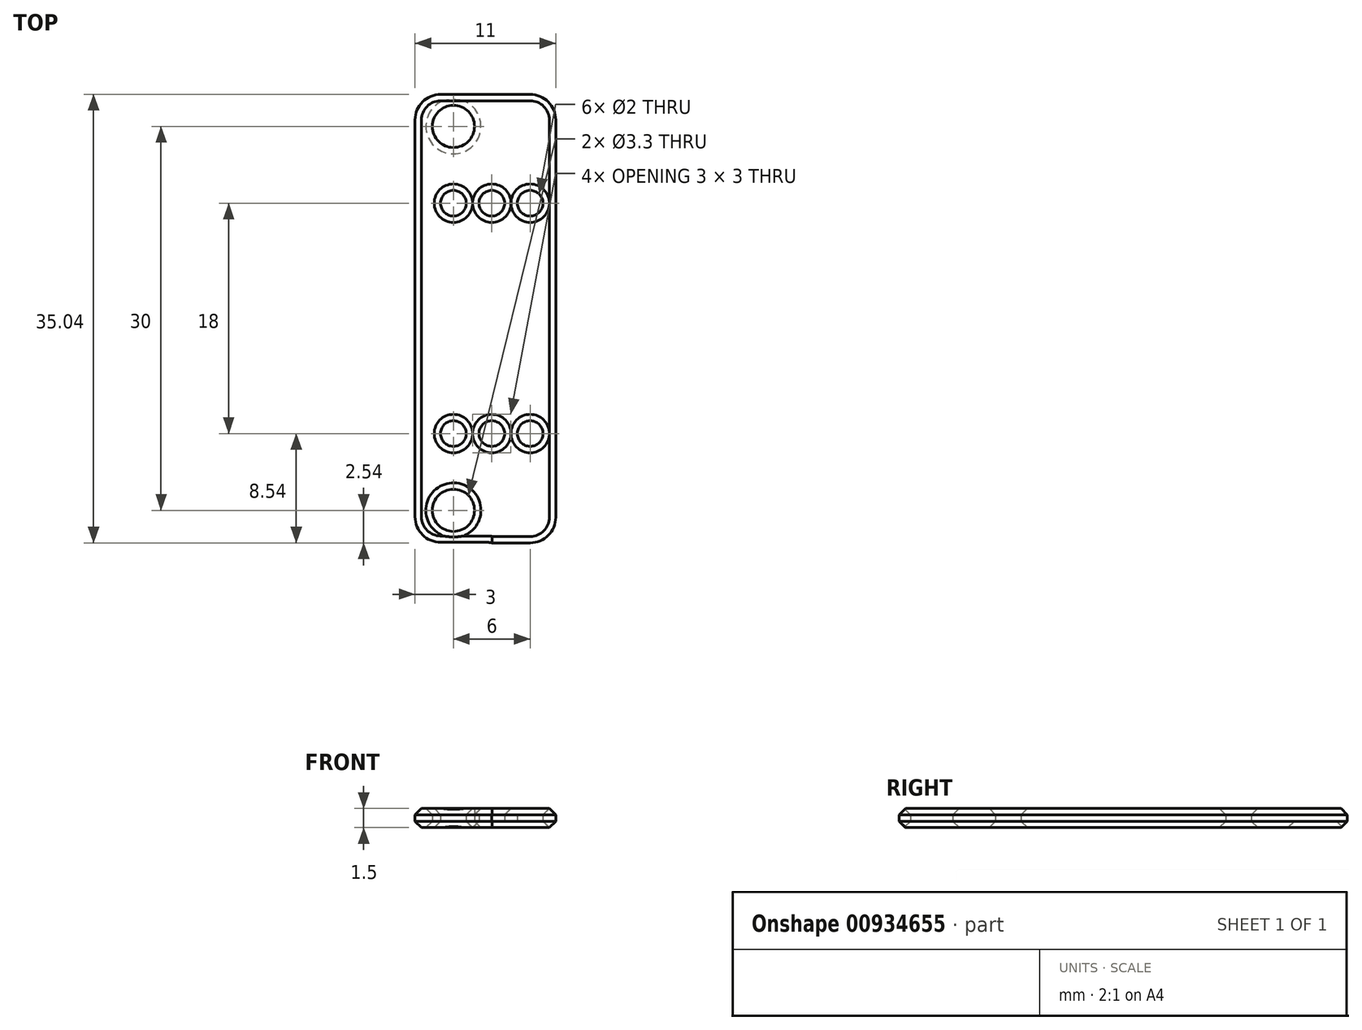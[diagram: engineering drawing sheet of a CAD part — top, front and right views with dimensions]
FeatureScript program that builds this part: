
annotation { "Feature Type Name" : "Feature", "Feature Type Description" : "" }
export const myFeature = defineFeature(function(context is Context, id is Id, definition is map)
    precondition{}
    {
        {
            var Q0;
            Q0=qCreatedBy(makeId("Top.planeOp"),FACE);
            var sketch = newSketch(context, id + "F0", { "sketchPlane" : qUnion([Q0])});
            skLineSegment(sketch, "E0.bottom", {"start": v(-3, 17.5) * mm, "end": v(3, 17.5) * mm});
            skLineSegment(sketch, "E0.top", {"start": v(-3, -17.5) * mm, "end": v(3, -17.5) * mm});
            skLineSegment(sketch, "E0.left", {"start": v(-3, 17.5) * mm, "end": v(-3, -17.5) * mm});
            skPoint(sketch, "E0.middle", {"position": v(0, 0) * mm});
            skCircle(sketch, "E1", {"center": v(0, 9) * mm, "radius": 1 * mm});
            skCircle(sketch, "E2", {"center": v(0, -9) * mm, "radius": 1 * mm});
            skCircle(sketch, "E3", {"center": v(0, 15) * mm, "radius": 1.65 * mm});
            skCircle(sketch, "E4", {"center": v(0, -15) * mm, "radius": 1.65 * mm});
            skLineSegment(sketch, "E5.bottom", {"start": v(3, 17.5) * mm, "end": v(8, 17.5) * mm});
            skLineSegment(sketch, "E5.top", {"start": v(3, -17.54) * mm, "end": v(8, -17.54) * mm});
            skLineSegment(sketch, "E5.left", {"start": v(3, -17.5) * mm, "end": v(3, -17.54) * mm});
            skLineSegment(sketch, "E5.right", {"start": v(8, 17.5) * mm, "end": v(8, -17.54) * mm});
            skCircle(sketch, "E6", {"center": v(3, 9) * mm, "radius": 1 * mm});
            skCircle(sketch, "E7", {"center": v(3, -9) * mm, "radius": 1 * mm});
            skCircle(sketch, "E8", {"center": v(6, 9) * mm, "radius": 1 * mm});
            skCircle(sketch, "E9", {"center": v(6, -9) * mm, "radius": 1 * mm});
            skSolve(sketch);
        }
        {
            var Q0;
            Q0=makeQuery(id+"F0.imprint","IMPRINT",FACE,{"disambiguationData":[TD([[makeQuery(id+"F0.imprint","IMPRINT",EDGE,{"derivedFrom":sQuery(id+"F0.wireOp",EDGE,"E0.bottom")}),-1.0]])]});
            extrude(context, id + "F1", {"entities" : qUnion([Q0]), "depth" : 1.5 * mm, "offsetDistance" : 25 * mm});
        }
        {
            var Q0;
            Q0=makeQuery(id+"F1.opExtrude","SWEPT_EDGE",EDGE,{"disambiguationData":[OSD([sQuery(id+"F0.wireOp",EDGE,"E0.bottom"),sQuery(id+"F0.wireOp",EDGE,"E0.left")])]});
            var Q1;
            Q1=makeQuery(id+"F1.opExtrude","SWEPT_EDGE",EDGE,{"disambiguationData":[OSD([sQuery(id+"F0.wireOp",EDGE,"E0.bottom"),sQuery(id+"F0.wireOp",EDGE,"E0.right")])]});
            var Q2;
            Q2=makeQuery(id+"F1.opExtrude","SWEPT_EDGE",EDGE,{"disambiguationData":[OSD([sQuery(id+"F0.wireOp",EDGE,"E0.top"),sQuery(id+"F0.wireOp",EDGE,"E0.left")])]});
            var Q3;
            Q3=makeQuery(id+"F1.opExtrude","SWEPT_EDGE",EDGE,{"disambiguationData":[OSD([sQuery(id+"F0.wireOp",EDGE,"E0.top"),sQuery(id+"F0.wireOp",EDGE,"E0.right")])]});
            var Q4;
            Q4=makeQuery(id+"F1.opExtrude","SWEPT_EDGE",EDGE,{"disambiguationData":[OSD([sQuery(id+"F0.wireOp",EDGE,"E5.bottom"),sQuery(id+"F0.wireOp",EDGE,"E5.right")])]});
            var Q5;
            Q5=makeQuery(id+"F1.opExtrude","SWEPT_EDGE",EDGE,{"disambiguationData":[OSD([sQuery(id+"F0.wireOp",EDGE,"E5.top"),sQuery(id+"F0.wireOp",EDGE,"E5.right")])]});
            fillet(context, id + "F2", {"entities" : qUnion([Q0, Q1, Q2, Q3, Q4, Q5]), "radius" : 2 * mm, "tangentPropagation" : true, "allowEdgeOverflow" : false});
        }
        {
            var Q0;
            Q0=makeQuery(id+"F1.opExtrude","CAP_EDGE",EDGE,{"disambiguationData":[OSD([sQuery(id+"F0.wireOp",EDGE,"E0.left")])],"isStart":false});
            var Q1;
            Q1=makeQuery(id+"F1.opExtrude","CAP_EDGE",EDGE,{"disambiguationData":[OSD([sQuery(id+"F0.wireOp",EDGE,"E0.right")])],"isStart":false});
            var Q2;
            {var subQ0=sQuery(id+"F0.wireOp",EDGE,"E0.right");var subQ1=sQuery(id+"F0.wireOp",EDGE,"E0.bottom");Q2=makeQuery(id+"F2.opFillet","BLEND_EDGE",EDGE,{"blendedFrom":[makeQuery(id+"F1.opExtrude","SWEPT_EDGE",EDGE,{"disambiguationData":[OSD([subQ1,subQ0])]}),makeQuery(id+"F1.opExtrude","CAP_FACE",FACE,{"disambiguationData":[OSD([subQ1,sQuery(id+"F0.wireOp",EDGE,"E0.top"),sQuery(id+"F0.wireOp",EDGE,"E0.left"),subQ0,sQuery(id+"F0.wireOp",EDGE,"E1"),sQuery(id+"F0.wireOp",EDGE,"E2"),sQuery(id+"F0.wireOp",EDGE,"E3"),sQuery(id+"F0.wireOp",EDGE,"E4")])],"isStart":false})],"blendedInto":[makeQuery(id+"F1.opExtrude","CAP_FACE",FACE,{"disambiguationData":[OSD([subQ1,sQuery(id+"F0.wireOp",EDGE,"E0.top"),sQuery(id+"F0.wireOp",EDGE,"E0.left"),subQ0,sQuery(id+"F0.wireOp",EDGE,"E1"),sQuery(id+"F0.wireOp",EDGE,"E2"),sQuery(id+"F0.wireOp",EDGE,"E3"),sQuery(id+"F0.wireOp",EDGE,"E4")])],"isStart":false})]});}
            var Q3;
            Q3=makeQuery(id+"F1.opExtrude","CAP_EDGE",EDGE,{"disambiguationData":[OSD([sQuery(id+"F0.wireOp",EDGE,"E0.bottom")])],"isStart":false});
            var Q4;
            {var subQ0=sQuery(id+"F0.wireOp",EDGE,"E0.left");var subQ1=sQuery(id+"F0.wireOp",EDGE,"E0.bottom");Q4=makeQuery(id+"F2.opFillet","BLEND_EDGE",EDGE,{"blendedFrom":[makeQuery(id+"F1.opExtrude","SWEPT_EDGE",EDGE,{"disambiguationData":[OSD([subQ1,subQ0])]}),makeQuery(id+"F1.opExtrude","CAP_FACE",FACE,{"disambiguationData":[OSD([subQ1,sQuery(id+"F0.wireOp",EDGE,"E0.top"),subQ0,sQuery(id+"F0.wireOp",EDGE,"E0.right"),sQuery(id+"F0.wireOp",EDGE,"E1"),sQuery(id+"F0.wireOp",EDGE,"E2"),sQuery(id+"F0.wireOp",EDGE,"E3"),sQuery(id+"F0.wireOp",EDGE,"E4")])],"isStart":false})],"blendedInto":[makeQuery(id+"F1.opExtrude","CAP_FACE",FACE,{"disambiguationData":[OSD([subQ1,sQuery(id+"F0.wireOp",EDGE,"E0.top"),subQ0,sQuery(id+"F0.wireOp",EDGE,"E0.right"),sQuery(id+"F0.wireOp",EDGE,"E1"),sQuery(id+"F0.wireOp",EDGE,"E2"),sQuery(id+"F0.wireOp",EDGE,"E3"),sQuery(id+"F0.wireOp",EDGE,"E4")])],"isStart":false})]});}
            var Q5;
            {var subQ0=sQuery(id+"F0.wireOp",EDGE,"E0.left");var subQ1=sQuery(id+"F0.wireOp",EDGE,"E0.top");Q5=makeQuery(id+"F2.opFillet","BLEND_EDGE",EDGE,{"blendedFrom":[makeQuery(id+"F1.opExtrude","SWEPT_EDGE",EDGE,{"disambiguationData":[OSD([subQ1,subQ0])]}),makeQuery(id+"F1.opExtrude","CAP_FACE",FACE,{"disambiguationData":[OSD([sQuery(id+"F0.wireOp",EDGE,"E0.bottom"),subQ1,subQ0,sQuery(id+"F0.wireOp",EDGE,"E0.right"),sQuery(id+"F0.wireOp",EDGE,"E1"),sQuery(id+"F0.wireOp",EDGE,"E2"),sQuery(id+"F0.wireOp",EDGE,"E3"),sQuery(id+"F0.wireOp",EDGE,"E4")])],"isStart":false})],"blendedInto":[makeQuery(id+"F1.opExtrude","CAP_FACE",FACE,{"disambiguationData":[OSD([sQuery(id+"F0.wireOp",EDGE,"E0.bottom"),subQ1,subQ0,sQuery(id+"F0.wireOp",EDGE,"E0.right"),sQuery(id+"F0.wireOp",EDGE,"E1"),sQuery(id+"F0.wireOp",EDGE,"E2"),sQuery(id+"F0.wireOp",EDGE,"E3"),sQuery(id+"F0.wireOp",EDGE,"E4")])],"isStart":false})]});}
            var Q6;
            Q6=makeQuery(id+"F1.opExtrude","CAP_EDGE",EDGE,{"disambiguationData":[OSD([sQuery(id+"F0.wireOp",EDGE,"E0.top")])],"isStart":false});
            var Q7;
            {var subQ0=sQuery(id+"F0.wireOp",EDGE,"E0.right");var subQ1=sQuery(id+"F0.wireOp",EDGE,"E0.top");Q7=makeQuery(id+"F2.opFillet","BLEND_EDGE",EDGE,{"blendedFrom":[makeQuery(id+"F1.opExtrude","SWEPT_EDGE",EDGE,{"disambiguationData":[OSD([subQ1,subQ0])]}),makeQuery(id+"F1.opExtrude","CAP_FACE",FACE,{"disambiguationData":[OSD([sQuery(id+"F0.wireOp",EDGE,"E0.bottom"),subQ1,sQuery(id+"F0.wireOp",EDGE,"E0.left"),subQ0,sQuery(id+"F0.wireOp",EDGE,"E1"),sQuery(id+"F0.wireOp",EDGE,"E2"),sQuery(id+"F0.wireOp",EDGE,"E3"),sQuery(id+"F0.wireOp",EDGE,"E4")])],"isStart":false})],"blendedInto":[makeQuery(id+"F1.opExtrude","CAP_FACE",FACE,{"disambiguationData":[OSD([sQuery(id+"F0.wireOp",EDGE,"E0.bottom"),subQ1,sQuery(id+"F0.wireOp",EDGE,"E0.left"),subQ0,sQuery(id+"F0.wireOp",EDGE,"E1"),sQuery(id+"F0.wireOp",EDGE,"E2"),sQuery(id+"F0.wireOp",EDGE,"E3"),sQuery(id+"F0.wireOp",EDGE,"E4")])],"isStart":false})]});}
            var Q8;
            {var subQ0=sQuery(id+"F0.wireOp",EDGE,"E0.left");var subQ1=sQuery(id+"F0.wireOp",EDGE,"E0.bottom");Q8=makeQuery(id+"F2.opFillet","BLEND_EDGE",EDGE,{"blendedFrom":[makeQuery(id+"F1.opExtrude","SWEPT_EDGE",EDGE,{"disambiguationData":[OSD([subQ1,subQ0])]}),makeQuery(id+"F1.opExtrude","CAP_FACE",FACE,{"disambiguationData":[OSD([subQ1,sQuery(id+"F0.wireOp",EDGE,"E0.top"),subQ0,sQuery(id+"F0.wireOp",EDGE,"E0.right"),sQuery(id+"F0.wireOp",EDGE,"E1"),sQuery(id+"F0.wireOp",EDGE,"E2"),sQuery(id+"F0.wireOp",EDGE,"E3"),sQuery(id+"F0.wireOp",EDGE,"E4")])],"isStart":true})],"blendedInto":[makeQuery(id+"F1.opExtrude","CAP_FACE",FACE,{"disambiguationData":[OSD([subQ1,sQuery(id+"F0.wireOp",EDGE,"E0.top"),subQ0,sQuery(id+"F0.wireOp",EDGE,"E0.right"),sQuery(id+"F0.wireOp",EDGE,"E1"),sQuery(id+"F0.wireOp",EDGE,"E2"),sQuery(id+"F0.wireOp",EDGE,"E3"),sQuery(id+"F0.wireOp",EDGE,"E4")])],"isStart":true})]});}
            var Q9;
            Q9=makeQuery(id+"F1.opExtrude","CAP_EDGE",EDGE,{"disambiguationData":[OSD([sQuery(id+"F0.wireOp",EDGE,"E0.bottom")])],"isStart":true});
            var Q10;
            {var subQ0=sQuery(id+"F0.wireOp",EDGE,"E0.right");var subQ1=sQuery(id+"F0.wireOp",EDGE,"E0.bottom");Q10=makeQuery(id+"F2.opFillet","BLEND_EDGE",EDGE,{"blendedFrom":[makeQuery(id+"F1.opExtrude","SWEPT_EDGE",EDGE,{"disambiguationData":[OSD([subQ1,subQ0])]}),makeQuery(id+"F1.opExtrude","CAP_FACE",FACE,{"disambiguationData":[OSD([subQ1,sQuery(id+"F0.wireOp",EDGE,"E0.top"),sQuery(id+"F0.wireOp",EDGE,"E0.left"),subQ0,sQuery(id+"F0.wireOp",EDGE,"E1"),sQuery(id+"F0.wireOp",EDGE,"E2"),sQuery(id+"F0.wireOp",EDGE,"E3"),sQuery(id+"F0.wireOp",EDGE,"E4")])],"isStart":true})],"blendedInto":[makeQuery(id+"F1.opExtrude","CAP_FACE",FACE,{"disambiguationData":[OSD([subQ1,sQuery(id+"F0.wireOp",EDGE,"E0.top"),sQuery(id+"F0.wireOp",EDGE,"E0.left"),subQ0,sQuery(id+"F0.wireOp",EDGE,"E1"),sQuery(id+"F0.wireOp",EDGE,"E2"),sQuery(id+"F0.wireOp",EDGE,"E3"),sQuery(id+"F0.wireOp",EDGE,"E4")])],"isStart":true})]});}
            var Q11;
            Q11=makeQuery(id+"F1.opExtrude","CAP_EDGE",EDGE,{"disambiguationData":[OSD([sQuery(id+"F0.wireOp",EDGE,"E0.right")])],"isStart":true});
            var Q12;
            Q12=makeQuery(id+"F1.opExtrude","CAP_EDGE",EDGE,{"disambiguationData":[OSD([sQuery(id+"F0.wireOp",EDGE,"E0.left")])],"isStart":true});
            var Q13;
            {var subQ0=sQuery(id+"F0.wireOp",EDGE,"E0.left");var subQ1=sQuery(id+"F0.wireOp",EDGE,"E0.top");Q13=makeQuery(id+"F2.opFillet","BLEND_EDGE",EDGE,{"blendedFrom":[makeQuery(id+"F1.opExtrude","SWEPT_EDGE",EDGE,{"disambiguationData":[OSD([subQ1,subQ0])]}),makeQuery(id+"F1.opExtrude","CAP_FACE",FACE,{"disambiguationData":[OSD([sQuery(id+"F0.wireOp",EDGE,"E0.bottom"),subQ1,subQ0,sQuery(id+"F0.wireOp",EDGE,"E0.right"),sQuery(id+"F0.wireOp",EDGE,"E1"),sQuery(id+"F0.wireOp",EDGE,"E2"),sQuery(id+"F0.wireOp",EDGE,"E3"),sQuery(id+"F0.wireOp",EDGE,"E4")])],"isStart":true})],"blendedInto":[makeQuery(id+"F1.opExtrude","CAP_FACE",FACE,{"disambiguationData":[OSD([sQuery(id+"F0.wireOp",EDGE,"E0.bottom"),subQ1,subQ0,sQuery(id+"F0.wireOp",EDGE,"E0.right"),sQuery(id+"F0.wireOp",EDGE,"E1"),sQuery(id+"F0.wireOp",EDGE,"E2"),sQuery(id+"F0.wireOp",EDGE,"E3"),sQuery(id+"F0.wireOp",EDGE,"E4")])],"isStart":true})]});}
            var Q14;
            Q14=makeQuery(id+"F1.opExtrude","CAP_EDGE",EDGE,{"disambiguationData":[OSD([sQuery(id+"F0.wireOp",EDGE,"E0.top")])],"isStart":true});
            var Q15;
            {var subQ0=sQuery(id+"F0.wireOp",EDGE,"E0.right");var subQ1=sQuery(id+"F0.wireOp",EDGE,"E0.top");Q15=makeQuery(id+"F2.opFillet","BLEND_EDGE",EDGE,{"blendedFrom":[makeQuery(id+"F1.opExtrude","SWEPT_EDGE",EDGE,{"disambiguationData":[OSD([subQ1,subQ0])]}),makeQuery(id+"F1.opExtrude","CAP_FACE",FACE,{"disambiguationData":[OSD([sQuery(id+"F0.wireOp",EDGE,"E0.bottom"),subQ1,sQuery(id+"F0.wireOp",EDGE,"E0.left"),subQ0,sQuery(id+"F0.wireOp",EDGE,"E1"),sQuery(id+"F0.wireOp",EDGE,"E2"),sQuery(id+"F0.wireOp",EDGE,"E3"),sQuery(id+"F0.wireOp",EDGE,"E4")])],"isStart":true})],"blendedInto":[makeQuery(id+"F1.opExtrude","CAP_FACE",FACE,{"disambiguationData":[OSD([sQuery(id+"F0.wireOp",EDGE,"E0.bottom"),subQ1,sQuery(id+"F0.wireOp",EDGE,"E0.left"),subQ0,sQuery(id+"F0.wireOp",EDGE,"E1"),sQuery(id+"F0.wireOp",EDGE,"E2"),sQuery(id+"F0.wireOp",EDGE,"E3"),sQuery(id+"F0.wireOp",EDGE,"E4")])],"isStart":true})]});}
            var Q16;
            Q16=makeQuery(id+"F1.opExtrude","CAP_EDGE",EDGE,{"disambiguationData":[OSD([sQuery(id+"F0.wireOp",EDGE,"E2")])],"isStart":true});
            var Q17;
            Q17=makeQuery(id+"F1.opExtrude","CAP_EDGE",EDGE,{"disambiguationData":[OSD([sQuery(id+"F0.wireOp",EDGE,"E1")])],"isStart":true});
            var Q18;
            Q18=makeQuery(id+"F1.opExtrude","CAP_EDGE",EDGE,{"disambiguationData":[OSD([sQuery(id+"F0.wireOp",EDGE,"E3")])],"isStart":true});
            var Q19;
            Q19=makeQuery(id+"F1.opExtrude","CAP_EDGE",EDGE,{"disambiguationData":[OSD([sQuery(id+"F0.wireOp",EDGE,"E2")])],"isStart":false});
            var Q20;
            Q20=makeQuery(id+"F1.opExtrude","CAP_EDGE",EDGE,{"disambiguationData":[OSD([sQuery(id+"F0.wireOp",EDGE,"E4")])],"isStart":false});
            var Q21;
            Q21=makeQuery(id+"F1.opExtrude","CAP_EDGE",EDGE,{"disambiguationData":[OSD([sQuery(id+"F0.wireOp",EDGE,"E4")])],"isStart":true});
            var Q22;
            Q22=makeQuery(id+"F1.opExtrude","CAP_EDGE",EDGE,{"disambiguationData":[OSD([sQuery(id+"F0.wireOp",EDGE,"E7")])],"isStart":false});
            var Q23;
            Q23=makeQuery(id+"F1.opExtrude","CAP_EDGE",EDGE,{"disambiguationData":[OSD([sQuery(id+"F0.wireOp",EDGE,"E9")])],"isStart":false});
            var Q24;
            Q24=makeQuery(id+"F1.opExtrude","CAP_EDGE",EDGE,{"disambiguationData":[OSD([sQuery(id+"F0.wireOp",EDGE,"E8")])],"isStart":false});
            var Q25;
            Q25=makeQuery(id+"F1.opExtrude","CAP_EDGE",EDGE,{"disambiguationData":[OSD([sQuery(id+"F0.wireOp",EDGE,"E6")])],"isStart":false});
            var Q26;
            Q26=makeQuery(id+"F1.opExtrude","CAP_EDGE",EDGE,{"disambiguationData":[OSD([sQuery(id+"F0.wireOp",EDGE,"E1")])],"isStart":false});
            var Q27;
            Q27=makeQuery(id+"F1.opExtrude","CAP_EDGE",EDGE,{"disambiguationData":[OSD([sQuery(id+"F0.wireOp",EDGE,"E8")])],"isStart":true});
            var Q28;
            Q28=makeQuery(id+"F1.opExtrude","CAP_EDGE",EDGE,{"disambiguationData":[OSD([sQuery(id+"F0.wireOp",EDGE,"E6")])],"isStart":true});
            var Q29;
            Q29=makeQuery(id+"F1.opExtrude","CAP_EDGE",EDGE,{"disambiguationData":[OSD([sQuery(id+"F0.wireOp",EDGE,"E7")])],"isStart":true});
            var Q30;
            Q30=makeQuery(id+"F1.opExtrude","CAP_EDGE",EDGE,{"disambiguationData":[OSD([sQuery(id+"F0.wireOp",EDGE,"E9")])],"isStart":true});
            chamfer(context, id + "F3", {"entities" : qUnion([Q0, Q1, Q2, Q3, Q4, Q5, Q6, Q7, Q8, Q9, Q10, Q11, Q12, Q13, Q14, Q15, Q16, Q17, Q18, Q19, Q20, Q21, Q22, Q23, Q24, Q25, Q26, Q27, Q28, Q29, Q30]), "width" : 0.5 * mm, "tangentPropagation" : true});
        }
    });
